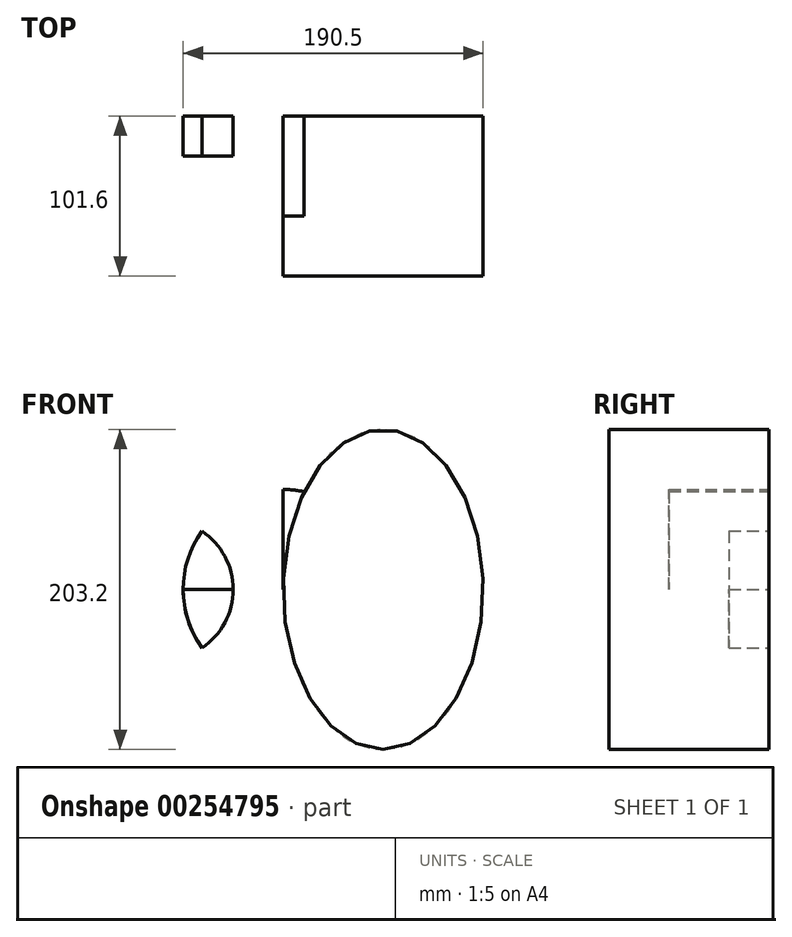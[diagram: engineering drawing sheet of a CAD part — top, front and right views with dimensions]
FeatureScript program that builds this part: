
annotation { "Feature Type Name" : "Feature", "Feature Type Description" : "" }
export const myFeature = defineFeature(function(context is Context, id is Id, definition is map)
    precondition{}
    {
        {
            var Q0;
            Q0=qCreatedBy(makeId("Front.planeOp"),FACE);
            var sketch = newSketch(context, id + "F0", { "sketchPlane" : qUnion([Q0])});
            skLineSegment(sketch, "E0", {"start": v(0, 0) * mm, "end": v(-76.2, 0) * mm});
            skCircle(sketch, "E1", {"center": v(-76.2, 0) * mm, "radius": 44.45 * mm});
            skLineSegment(sketch, "E2", {"start": v(-76.2, 0) * mm, "end": v(-63.5, 0) * mm});
            skCircle(sketch, "E3", {"center": v(0, 0) * mm, "radius": 63.5 * mm});
            skLineSegment(sketch, "E4", {"start": v(0, 0) * mm, "end": v(0, 101.6) * mm});
            skLineSegment(sketch, "E5", {"start": v(63.5, 0) * mm, "end": v(63.5, 101.6) * mm});
            skLineSegment(sketch, "E6", {"start": v(0, 101.6) * mm, "end": v(99.08, 101.6) * mm});
            skEllipse(sketch, "E7", {"center": v(63.5, 0) * mm, "majorRadius": 63.5 * mm, "minorRadius": 101.6 * mm, "majorAxis": v(-1, 0)});
            skSolve(sketch);
        }
        {
            var Q0;
            {var subQ0=sQuery(id+"F0.wireOp",EDGE,"E3");var subQ1=sQuery(id+"F0.wireOp",EDGE,"E1");var subQ2=makeQuery(id+"F0.imprint","INTERSECT",VERTEX,{"disambiguationData":[OD(0.0)],"derivedFrom":[subQ1,subQ0]});Q0=makeQuery(id+"F0.imprint","IMPRINT",FACE,{"disambiguationData":[TD([[makeQuery(id+"F0.imprint","IMPRINT",EDGE,{"disambiguationData":[TD([[subQ2,-1.0]])],"derivedFrom":subQ1}),1.0]])]});}
            extrude(context, id + "F1", {"entities" : qUnion([Q0]), "depth" : 25.4 * mm});
        }
        {
            var Q0;
            {var subQ3=sQuery(id+"F0.wireOp",EDGE,"E1");var subQ5=sQuery(id+"F0.wireOp",EDGE,"E3");var subQ6=makeQuery(id+"F0.imprint","INTERSECT",VERTEX,{"disambiguationData":[OD(0.0)],"derivedFrom":[subQ3,subQ5]});Q0=makeQuery(id+"F0.imprint","IMPRINT",FACE,{"disambiguationData":[TD([[makeQuery(id+"F0.imprint","IMPRINT",EDGE,{"disambiguationData":[TD([[subQ6,1.0]])],"derivedFrom":subQ3}),-1.0]])]});}
            var Q1;
            {var subQ3=sQuery(id+"F0.wireOp",EDGE,"E1");var subQ5=sQuery(id+"F0.wireOp",EDGE,"E3");var subQ7=makeQuery(id+"F0.imprint","INTERSECT",VERTEX,{"disambiguationData":[OD(1.0)],"derivedFrom":[subQ3,subQ5]});Q1=makeQuery(id+"F0.imprint","IMPRINT",FACE,{"disambiguationData":[TD([[makeQuery(id+"F0.imprint","IMPRINT",EDGE,{"disambiguationData":[TD([[subQ7,-1.0]])],"derivedFrom":subQ3}),-1.0]])]});}
            var Q2;
            {var subQ0=sQuery(id+"F0.wireOp",EDGE,"E4");var subQ1=sQuery(id+"F0.wireOp",EDGE,"E3");var subQ2=makeQuery(id+"F0.imprint","INTERSECT",VERTEX,{"derivedFrom":[subQ1,subQ0]});Q2=makeQuery(id+"F0.imprint","IMPRINT",FACE,{"disambiguationData":[TD([[makeQuery(id+"F0.imprint","IMPRINT",EDGE,{"disambiguationData":[TD([[subQ2,1.0]])],"derivedFrom":subQ1}),1.0]])]});}
            extrude(context, id + "F2", {"entities" : qUnion([Q0, Q1, Q2]), "depth" : 63.5 * mm});
        }
        {
            var Q0;
            {var subQ0=sQuery(id+"F0.wireOp",EDGE,"E5");Q0=makeQuery(id+"F0.imprint","IMPRINT",FACE,{"disambiguationData":[TD([[makeQuery(id+"F0.imprint","IMPRINT",EDGE,{"derivedFrom":subQ0}),1.0]])]});}
            var Q1;
            {var subQ0=sQuery(id+"F0.wireOp",EDGE,"E3");var subQ1=makeQuery(id+"F0.imprint","INTERSECT",VERTEX,{"derivedFrom":[subQ0,sQuery(id+"F0.wireOp",EDGE,"E5")]});Q1=makeQuery(id+"F0.imprint","IMPRINT",FACE,{"disambiguationData":[TD([[makeQuery(id+"F0.imprint","IMPRINT",EDGE,{"disambiguationData":[TD([[subQ1,-1.0]])],"derivedFrom":subQ0}),1.0]])]});}
            var Q2;
            {var subQ0=sQuery(id+"F0.wireOp",EDGE,"E5");Q2=makeQuery(id+"F0.imprint","IMPRINT",FACE,{"disambiguationData":[TD([[makeQuery(id+"F0.imprint","IMPRINT",EDGE,{"derivedFrom":subQ0}),-1.0]])]});}
            extrude(context, id + "F3", {"entities" : qUnion([Q0, Q1, Q2]), "operationType" : NewBodyOperationType.ADD, "depth" : 101.6 * mm});
        }
        {
            var Q0;
            {var subQ0=sQuery(id+"F0.wireOp",EDGE,"E3");var subQ1=sQuery(id+"F0.wireOp",EDGE,"E0");var subQ2=makeQuery(id+"F0.imprint","INTERSECT",VERTEX,{"derivedFrom":[subQ1,subQ0]});Q0=makeQuery(id+"F0.imprint","IMPRINT",FACE,{"disambiguationData":[TD([[makeQuery(id+"F0.imprint","IMPRINT",EDGE,{"disambiguationData":[TD([[subQ2,1.0]])],"derivedFrom":subQ1}),-1.0]])]});}
            var Q1;
            {var subQ0=sQuery(id+"F0.wireOp",EDGE,"E3");var subQ1=sQuery(id+"F0.wireOp",EDGE,"E0");var subQ2=makeQuery(id+"F0.imprint","INTERSECT",VERTEX,{"derivedFrom":[subQ1,subQ0]});Q1=makeQuery(id+"F0.imprint","IMPRINT",FACE,{"disambiguationData":[TD([[makeQuery(id+"F0.imprint","IMPRINT",EDGE,{"disambiguationData":[TD([[subQ2,1.0]])],"derivedFrom":subQ1}),1.0]])]});}
            extrude(context, id + "F4", {"entities" : qUnion([Q0, Q1]), "depth" : 25.4 * mm});
        }
    });
